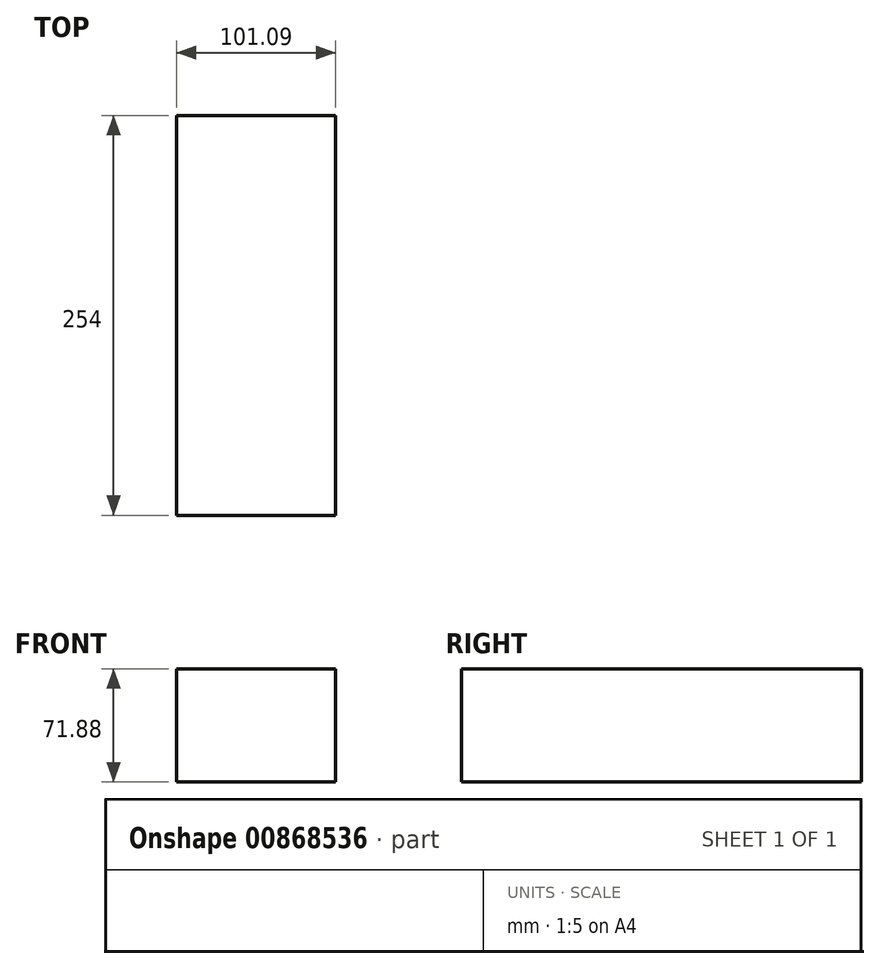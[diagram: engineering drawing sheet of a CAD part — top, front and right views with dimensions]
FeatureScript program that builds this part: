
annotation { "Feature Type Name" : "Feature", "Feature Type Description" : "" }
export const myFeature = defineFeature(function(context is Context, id is Id, definition is map)
    precondition{}
    {
        {
            var Q0;
            Q0=qCreatedBy(makeId("Front.planeOp"),FACE);
            var sketch = newSketch(context, id + "F0", { "sketchPlane" : qUnion([Q0])});
            skLineSegment(sketch, "E0.bottom", {"start": v(-63.14, 28.05) * mm, "end": v(37.95, 28.05) * mm});
            skLineSegment(sketch, "E0.top", {"start": v(-63.14, -43.83) * mm, "end": v(37.95, -43.83) * mm});
            skLineSegment(sketch, "E0.left", {"start": v(-63.14, 28.05) * mm, "end": v(-63.14, -43.83) * mm});
            skLineSegment(sketch, "E0.right", {"start": v(37.95, 28.05) * mm, "end": v(37.95, -43.83) * mm});
            skSolve(sketch);
        }
        {
            var Q0;
            Q0=makeQuery(id+"F0.imprint","IMPRINT",FACE,{"disambiguationData":[TD([[makeQuery(id+"F0.imprint","IMPRINT",EDGE,{"derivedFrom":sQuery(id+"F0.wireOp",EDGE,"E0.bottom")}),-1.0]])]});
            extrude(context, id + "F1", {"entities" : qUnion([Q0]), "depth" : 254 * mm, "offsetDistance" : 25.4 * mm});
        }
    });
